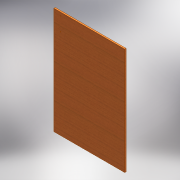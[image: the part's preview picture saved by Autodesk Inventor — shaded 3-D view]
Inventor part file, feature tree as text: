
AUTODESK INVENTOR PART (.ipt)
format: ipt  version: 2016 (Build 200138000, 138)  size: 139,264 bytes
history: native  units: mm
features: extrude x1, sketch x1
ambient origin geometry x8: Origin, YZ Plane, XZ Plane, XY Plane, X Axis, Y Axis, Z Axis, Center Point
bodies: Body1 (feature_tree)
feature tree (2):
  extrude  "Extrusion8"  Depth=10.0mm
  sketch  "Sketch8"  dims[d38=70.0mm d39=20.0mm d42=80.0mm d43=6.0mm d44=50.0mm d45=50.0mm d46=10.0mm d47=0.0mm d48=100.0mm d49=6.0mm]
